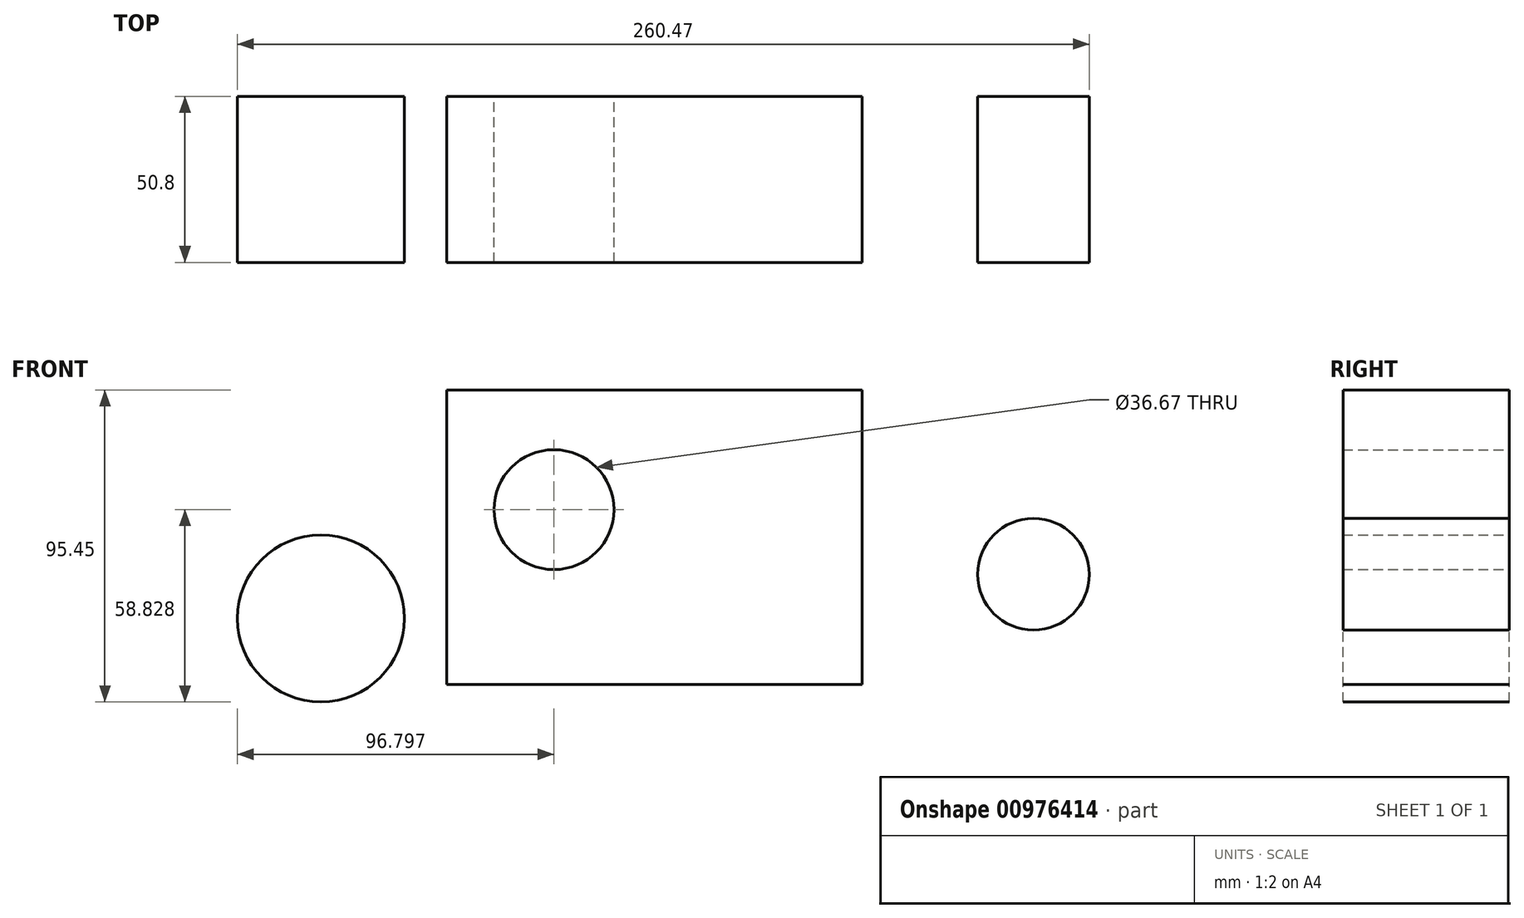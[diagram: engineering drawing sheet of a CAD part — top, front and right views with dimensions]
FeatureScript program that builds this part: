
annotation { "Feature Type Name" : "Feature", "Feature Type Description" : "" }
export const myFeature = defineFeature(function(context is Context, id is Id, definition is map)
    precondition{}
    {
        {
            var Q0;
            Q0=qCreatedBy(makeId("Front.planeOp"),FACE);
            var sketch = newSketch(context, id + "F0", { "sketchPlane" : qUnion([Q0])});
            skLineSegment(sketch, "E0.bottom", {"start": v(-59.43, 42.98) * mm, "end": v(67.57, 42.98) * mm});
            skLineSegment(sketch, "E0.top", {"start": v(-59.43, -47.16) * mm, "end": v(67.57, -47.16) * mm});
            skLineSegment(sketch, "E0.left", {"start": v(-59.43, 42.98) * mm, "end": v(-59.43, -47.16) * mm});
            skLineSegment(sketch, "E0.right", {"start": v(67.57, 42.98) * mm, "end": v(67.57, -47.16) * mm});
            skCircle(sketch, "E1", {"center": v(-26.64, 6.36) * mm, "radius": 18.34 * mm});
            skPoint(sketch, "E1.first.point", {"position": v(-38.5, 20.35) * mm});
            skPoint(sketch, "E1.second.point", {"position": v(-26.4, -11.98) * mm});
            skPoint(sketch, "E1.third.point", {"position": v(-43.84, 0) * mm});
            skCircle(sketch, "E2", {"center": v(-97.89, -26.92) * mm, "radius": 25.56 * mm});
            skPoint(sketch, "E2.first.point", {"position": v(-105.25, -2.44) * mm});
            skPoint(sketch, "E2.second.point", {"position": v(-72.68, -22.68) * mm});
            skPoint(sketch, "E2.third.point", {"position": v(-81.75, -7.1) * mm});
            skCircle(sketch, "E3", {"center": v(119.96, -13.4) * mm, "radius": 17.07 * mm});
            skPoint(sketch, "E3.first.point", {"position": v(123.15, 3.37) * mm});
            skPoint(sketch, "E3.second.point", {"position": v(122, -30.35) * mm});
            skPoint(sketch, "E3.third.point", {"position": v(102.92, -14.54) * mm});
            skSolve(sketch);
        }
        {
            var Q0;
            Q0 = qSketchRegion(id + "F0", true);
            extrude(context, id + "F1", {"entities" : qUnion([Q0]), "depth" : 50.8 * mm, "offsetDistance" : 25.4 * mm});
        }
    });
